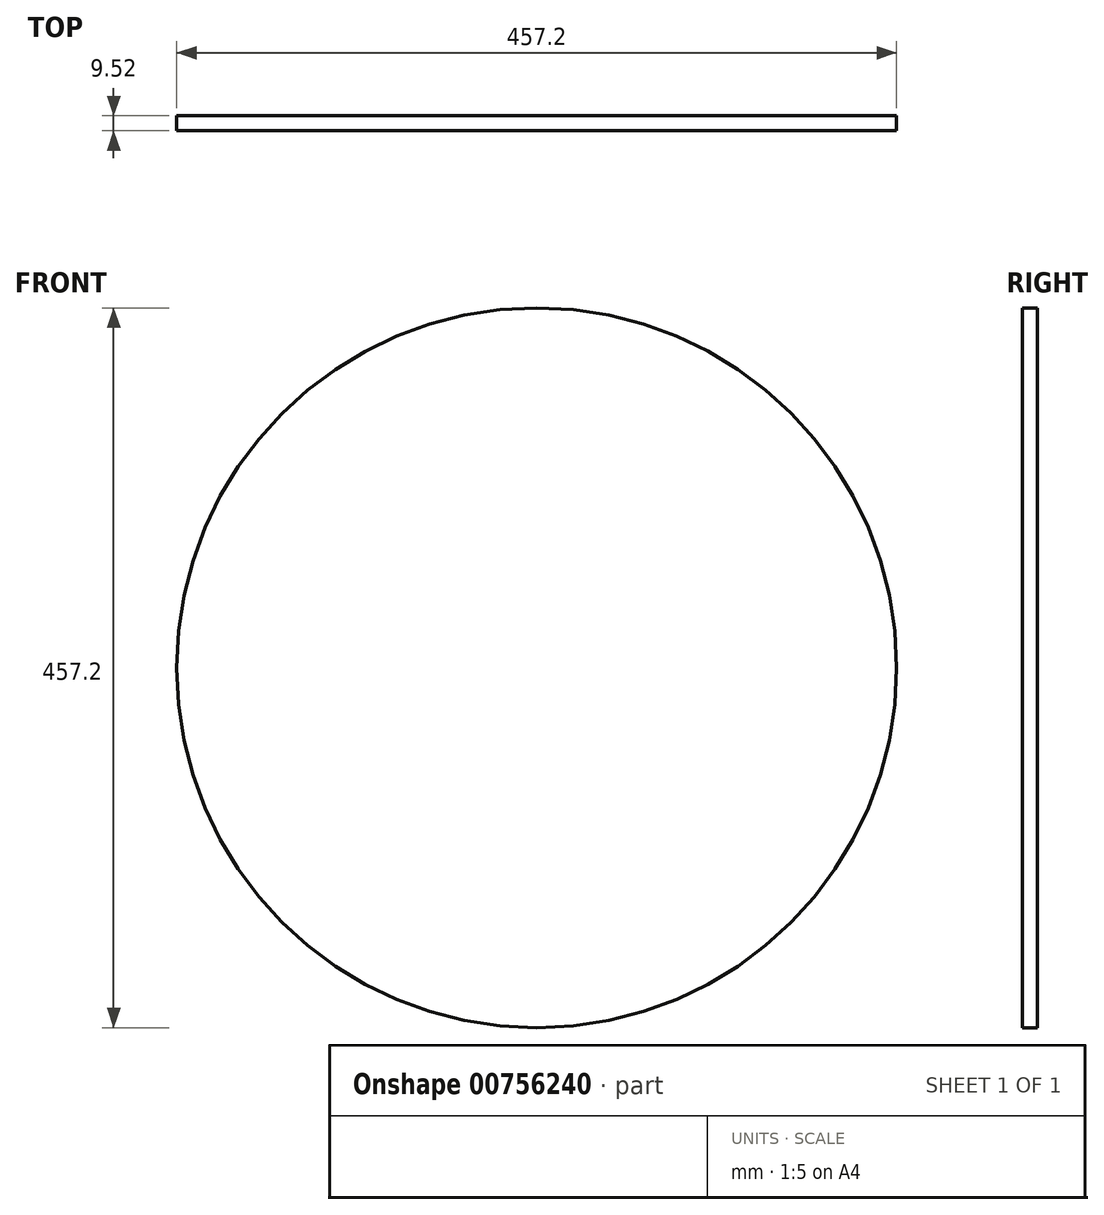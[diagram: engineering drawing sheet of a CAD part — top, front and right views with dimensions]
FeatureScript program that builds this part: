
annotation { "Feature Type Name" : "Feature", "Feature Type Description" : "" }
export const myFeature = defineFeature(function(context is Context, id is Id, definition is map)
    precondition{}
    {
        {
            var Q0;
            Q0=qCreatedBy(makeId("Front.planeOp"),FACE);
            var sketch = newSketch(context, id + "F0", { "sketchPlane" : qUnion([Q0])});
            skCircle(sketch, "E0", {"center": v(0, 0) * mm, "radius": 228.6 * mm});
            skArc(sketch, "E1", {"start": v(-228.57, 301.2) * mm, "mid": v(-3.69, 533.37) * mm, "end": v(228.57, 308.58) * mm});
            skLineSegment(sketch, "E2", {"start": v(-228.57, 301.2) * mm, "end": v(-228.57, 3.6) * mm});
            skLineSegment(sketch, "E3", {"start": v(228.57, 308.58) * mm, "end": v(228.6, 0) * mm});
            skSolve(sketch);
        }
        {
            var Q0;
            Q0=makeQuery(id+"F0.imprint","IMPRINT",FACE,{"disambiguationData":[TD([[makeQuery(id+"F0.imprint","IMPRINT",EDGE,{"derivedFrom":sQuery(id+"F0.wireOp",EDGE,"E1")}),-1.0]])]});
            var Q1;
            {var subQ0=sQuery(id+"F0.wireOp",EDGE,"E0");var subQ1=makeQuery(id+"F0.imprint","INTERSECT",VERTEX,{"derivedFrom":[subQ0,sQuery(id+"F0.wireOp",EDGE,"E2")]});Q1=makeQuery(id+"F0.imprint","IMPRINT",FACE,{"disambiguationData":[TD([[makeQuery(id+"F0.imprint","IMPRINT",EDGE,{"disambiguationData":[TD([[subQ1,1.0]])],"derivedFrom":subQ0}),1.0]])]});}
            extrude(context, id + "F1", {"entities" : qUnion([Q0, Q1]), "endBound" : BoundingType.SYMMETRIC, "depth" : 9.52 * mm, "offsetDistance" : 25.4 * mm});
        }
    });
